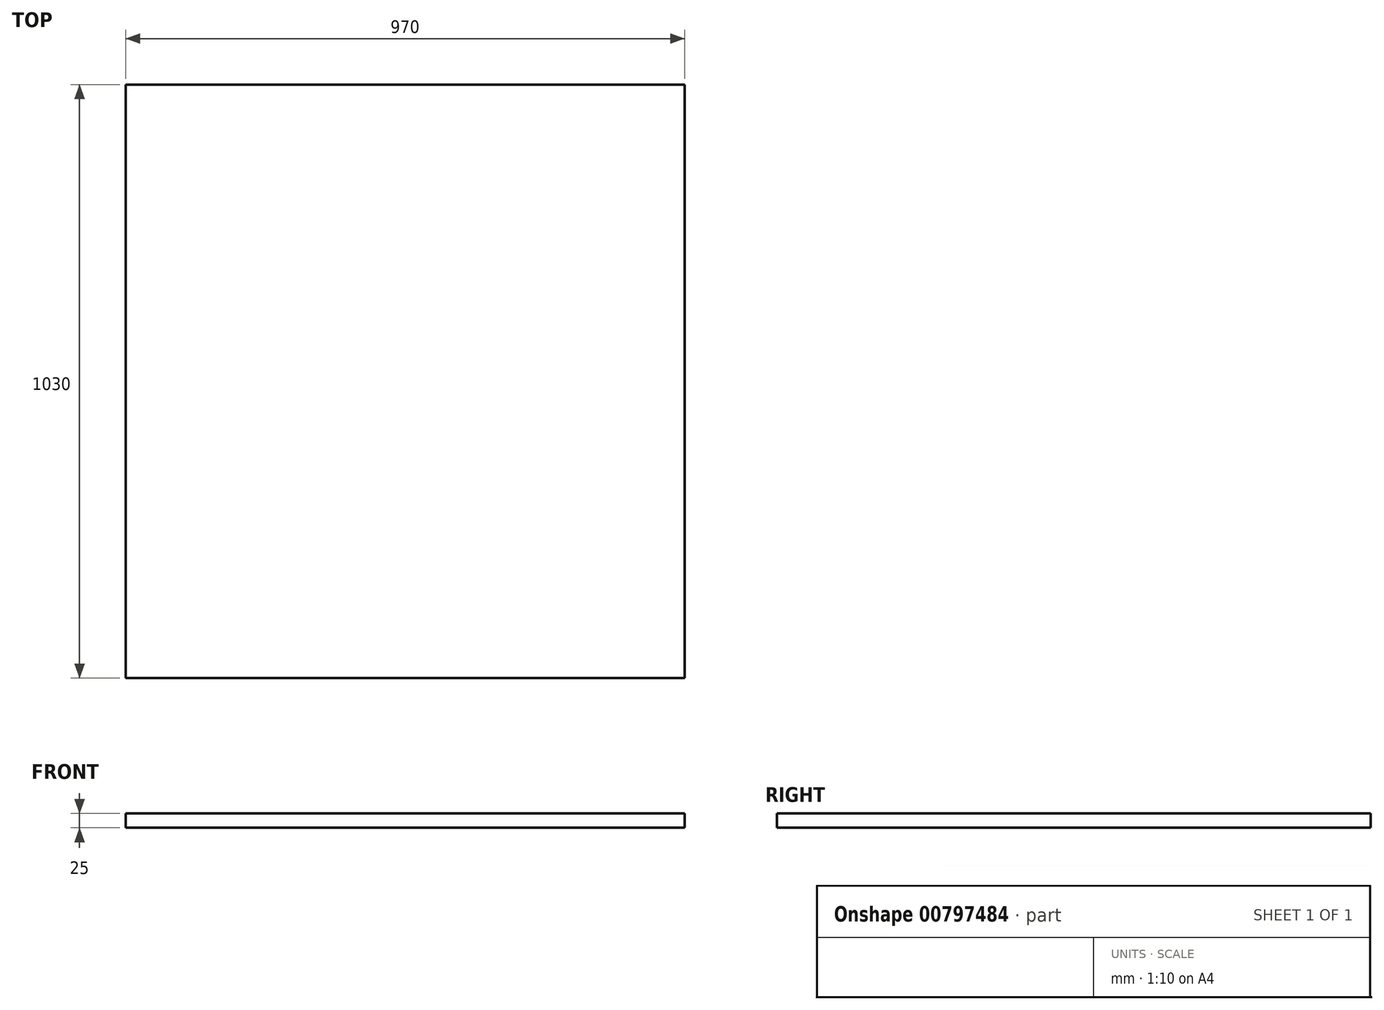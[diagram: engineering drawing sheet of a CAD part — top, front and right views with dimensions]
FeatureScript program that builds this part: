
annotation { "Feature Type Name" : "Feature", "Feature Type Description" : "" }
export const myFeature = defineFeature(function(context is Context, id is Id, definition is map)
    precondition{}
    {
        {
            var Q0;
            Q0=qCreatedBy(makeId("Top.planeOp"),FACE);
            var sketch = newSketch(context, id + "F0", { "sketchPlane" : qUnion([Q0])});
            skLineSegment(sketch, "E0.bottom", {"start": v(0, 0) * mm, "end": v(970, 0) * mm});
            skLineSegment(sketch, "E0.top", {"start": v(0, -1030) * mm, "end": v(970, -1030) * mm});
            skLineSegment(sketch, "E0.left", {"start": v(0, 0) * mm, "end": v(0, -1030) * mm});
            skLineSegment(sketch, "E0.right", {"start": v(970, 0) * mm, "end": v(970, -1030) * mm});
            skSolve(sketch);
        }
        {
            var Q0;
            Q0=makeQuery(id+"F0.imprint","IMPRINT",FACE,{"disambiguationData":[TD([[makeQuery(id+"F0.imprint","IMPRINT",EDGE,{"derivedFrom":sQuery(id+"F0.wireOp",EDGE,"E0.bottom")}),-1.0]])]});
            extrude(context, id + "F1", {"entities" : qUnion([Q0]), "depth" : 25 * mm, "offsetDistance" : 25 * mm});
        }
    });
